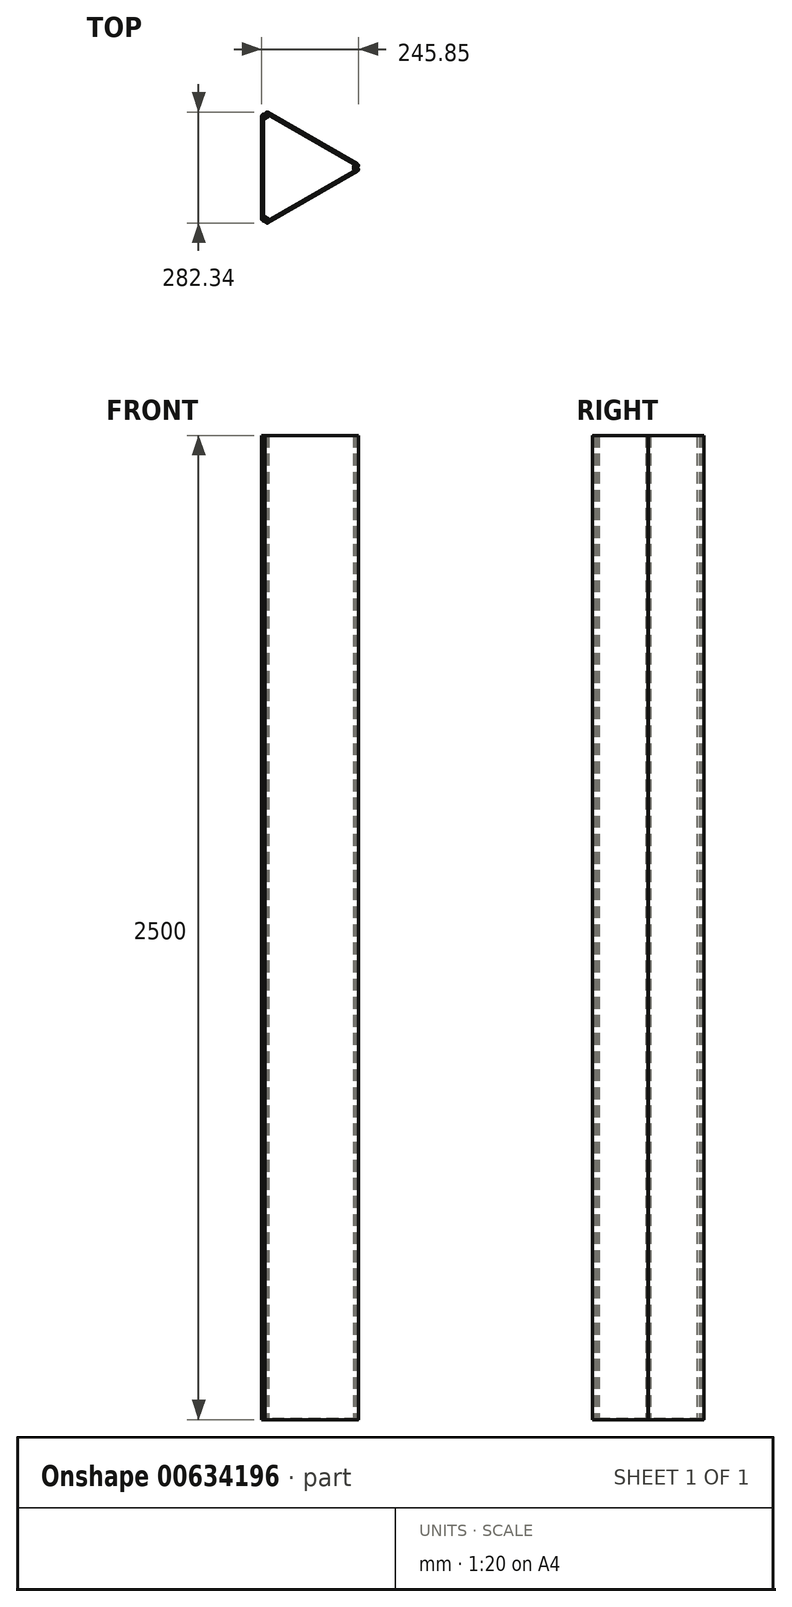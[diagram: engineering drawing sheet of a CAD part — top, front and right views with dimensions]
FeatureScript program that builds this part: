
annotation { "Feature Type Name" : "Feature", "Feature Type Description" : "" }
export const myFeature = defineFeature(function(context is Context, id is Id, definition is map)
    precondition{}
    {
        {
            var Q0;
            Q0=qCreatedBy(makeId("Top.planeOp"),FACE);
            var sketch = newSketch(context, id + "F0", { "sketchPlane" : qUnion([Q0])});
            skLineSegment(sketch, "E0", {"start": v(16.45, 140.5) * mm, "end": v(243.35, 9.5) * mm});
            skLineSegment(sketch, "E1", {"start": v(243.35, -9.5) * mm, "end": v(16.45, -140.5) * mm});
            skPoint(sketch, "E2.visualSharp", {"position": v(0, 150) * mm});
            skArc(sketch, "E2.filletArc", {"start": v(16.45, 140.5) * mm, "mid": v(10.42, 139.7) * mm, "end": v(9.62, 133.67) * mm});
            skLineSegment(sketch, "E3", {"start": v(0, -131) * mm, "end": v(0, 131) * mm});
            skArc(sketch, "E4.filletArc", {"start": v(9.33, 133.5) * mm, "mid": v(3.7, 135.83) * mm, "end": v(0, 131) * mm});
            skPoint(sketch, "E5.visualSharp", {"position": v(259.8, 0) * mm});
            skArc(sketch, "E5.filletArc", {"start": v(240.85, 0.17) * mm, "mid": v(245.68, 3.88) * mm, "end": v(243.35, 9.5) * mm});
            skPoint(sketch, "E6.visualSharp", {"position": v(0, -150) * mm});
            skArc(sketch, "E6.filletArc", {"start": v(0, -131) * mm, "mid": v(3.7, -135.83) * mm, "end": v(9.33, -133.5) * mm});
            skArc(sketch, "E7.filletArc", {"start": v(9.62, -133.67) * mm, "mid": v(10.42, -139.7) * mm, "end": v(16.45, -140.5) * mm});
            skArc(sketch, "E8.filletArc", {"start": v(243.35, -9.5) * mm, "mid": v(245.68, -3.88) * mm, "end": v(240.85, -0.17) * mm});
            skLineSegment(sketch, "E9", {"start": v(240.85, -0.17) * mm, "end": v(238.35, -0.17) * mm});
            skLineSegment(sketch, "E10", {"start": v(238.35, -0.17) * mm, "end": v(238.35, 0.17) * mm});
            skLineSegment(sketch, "E11", {"start": v(238.35, 0.17) * mm, "end": v(240.85, 0.17) * mm});
            skLineSegment(sketch, "E12", {"start": v(240.85, 5.17) * mm, "end": v(240.85, -5.17) * mm, "construction": true});
            skLineSegment(sketch, "E13", {"start": v(13.95, -136.17) * mm, "end": v(5, -131) * mm, "construction": true});
            skLineSegment(sketch, "E14", {"start": v(9.62, -133.67) * mm, "end": v(10.87, -131.5) * mm});
            skLineSegment(sketch, "E15", {"start": v(9.33, -133.5) * mm, "end": v(10.58, -131.33) * mm});
            skLineSegment(sketch, "E16", {"start": v(10.58, -131.33) * mm, "end": v(10.87, -131.5) * mm});
            skLineSegment(sketch, "E17", {"start": v(13.95, 136.17) * mm, "end": v(5, 131) * mm, "construction": true});
            skLineSegment(sketch, "E18", {"start": v(9.62, 133.67) * mm, "end": v(10.87, 131.5) * mm});
            skLineSegment(sketch, "E19", {"start": v(9.33, 133.5) * mm, "end": v(10.58, 131.33) * mm});
            skLineSegment(sketch, "E20", {"start": v(10.58, 131.33) * mm, "end": v(10.87, 131.5) * mm});
            skSolve(sketch);
        }
        {
            var Q0;
            Q0 = qSketchRegion(id + "F0", true);
            extrude(context, id + "F1", {"entities" : qUnion([Q0]), "depth" : 2500 * mm, "offsetDistance" : 25 * mm});
        }
        {
            var Q0;
            Q0=makeQuery(id+"F1.opExtrude","CAP_FACE",FACE,{"disambiguationData":[OSD([sQuery(id+"F0.wireOp",EDGE,"E0"),sQuery(id+"F0.wireOp",EDGE,"E1"),sQuery(id+"F0.wireOp",EDGE,"E2.filletArc"),sQuery(id+"F0.wireOp",EDGE,"E3"),sQuery(id+"F0.wireOp",EDGE,"E4.filletArc"),sQuery(id+"F0.wireOp",EDGE,"E5.filletArc"),sQuery(id+"F0.wireOp",EDGE,"E6.filletArc"),sQuery(id+"F0.wireOp",EDGE,"E7.filletArc"),sQuery(id+"F0.wireOp",EDGE,"E8.filletArc")])],"isStart":false});
            var Q1;
            Q1=makeQuery(id+"F1.opExtrude","CAP_FACE",FACE,{"disambiguationData":[OSD([sQuery(id+"F0.wireOp",EDGE,"E0"),sQuery(id+"F0.wireOp",EDGE,"E1"),sQuery(id+"F0.wireOp",EDGE,"E2.filletArc"),sQuery(id+"F0.wireOp",EDGE,"E3"),sQuery(id+"F0.wireOp",EDGE,"E4.filletArc"),sQuery(id+"F0.wireOp",EDGE,"E5.filletArc"),sQuery(id+"F0.wireOp",EDGE,"E6.filletArc"),sQuery(id+"F0.wireOp",EDGE,"E7.filletArc"),sQuery(id+"F0.wireOp",EDGE,"E8.filletArc")])],"isStart":true});
            var Q2;
            Q2=makeQuery(id+"F1.opExtrude","SWEPT_BODY",BODY,{"disambiguationData":[OSD([sQuery(id+"F0.wireOp",EDGE,"E0"),sQuery(id+"F0.wireOp",EDGE,"E1"),sQuery(id+"F0.wireOp",EDGE,"E2.filletArc"),sQuery(id+"F0.wireOp",EDGE,"E3"),sQuery(id+"F0.wireOp",EDGE,"E4.filletArc"),sQuery(id+"F0.wireOp",EDGE,"E5.filletArc"),sQuery(id+"F0.wireOp",EDGE,"E6.filletArc"),sQuery(id+"F0.wireOp",EDGE,"E7.filletArc"),sQuery(id+"F0.wireOp",EDGE,"E8.filletArc")])]});
            shell(context, id + "F2", {"entities" : qUnion([Q0, Q1]), "parts" : qUnion([Q2]), "thickness" : 5 * mm});
        }
        {
            var Q0;
            Q0=makeQuery(id+"F1.opExtrude","CAP_FACE",FACE,{"disambiguationData":[OSD([sQuery(id+"F0.wireOp",EDGE,"E0"),sQuery(id+"F0.wireOp",EDGE,"E1"),sQuery(id+"F0.wireOp",EDGE,"E2.filletArc"),sQuery(id+"F0.wireOp",EDGE,"E3"),sQuery(id+"F0.wireOp",EDGE,"E4.filletArc"),sQuery(id+"F0.wireOp",EDGE,"E5.filletArc"),sQuery(id+"F0.wireOp",EDGE,"E6.filletArc"),sQuery(id+"F0.wireOp",EDGE,"E7.filletArc"),sQuery(id+"F0.wireOp",EDGE,"E8.filletArc"),sQuery(id+"F0.wireOp",EDGE,"E9"),sQuery(id+"F0.wireOp",EDGE,"E10"),sQuery(id+"F0.wireOp",EDGE,"E11"),sQuery(id+"F0.wireOp",EDGE,"E14"),sQuery(id+"F0.wireOp",EDGE,"E15"),sQuery(id+"F0.wireOp",EDGE,"E16"),sQuery(id+"F0.wireOp",EDGE,"E18"),sQuery(id+"F0.wireOp",EDGE,"E19"),sQuery(id+"F0.wireOp",EDGE,"E20")])],"isStart":true});
            var sketch = newSketch(context, id + "F3", { "sketchPlane" : qUnion([Q0])});
            skLineSegment(sketch, "E21.0", {"start": v(5, 131) * mm, "end": v(5, -131) * mm});
            skLineSegment(sketch, "E21.1", {"start": v(5, -131) * mm, "end": v(8.75, -124.5) * mm});
            skLineSegment(sketch, "E21.2", {"start": v(8.75, -124.5) * mm, "end": v(17.7, -129.67) * mm});
            skLineSegment(sketch, "E21.3", {"start": v(13.95, -136.17) * mm, "end": v(17.7, -129.67) * mm});
            skLineSegment(sketch, "E21.4", {"start": v(13.95, -136.17) * mm, "end": v(240.85, -5.17) * mm});
            skLineSegment(sketch, "E21.5", {"start": v(233.35, -5.17) * mm, "end": v(240.85, -5.17) * mm});
            skLineSegment(sketch, "E21.6", {"start": v(233.35, 5.17) * mm, "end": v(233.35, -5.17) * mm});
            skLineSegment(sketch, "E21.7", {"start": v(240.85, 5.17) * mm, "end": v(233.35, 5.17) * mm});
            skLineSegment(sketch, "E21.8", {"start": v(240.85, 5.17) * mm, "end": v(13.95, 136.17) * mm});
            skLineSegment(sketch, "E21.9", {"start": v(5, 131) * mm, "end": v(8.75, 124.5) * mm});
            skLineSegment(sketch, "E21.10", {"start": v(8.75, 124.5) * mm, "end": v(17.7, 129.67) * mm});
            skLineSegment(sketch, "E21.11", {"start": v(13.95, 136.17) * mm, "end": v(17.7, 129.67) * mm});
            skPoint(sketch, "E21.12", {"position": v(6.87, -127.75) * mm});
            skPoint(sketch, "E21.13", {"position": v(15.83, -132.92) * mm});
            skSolve(sketch);
        }
        {
            var Q0;
            Q0 = qSketchRegion(id + "F3", true);
            extrude(context, id + "F4", {"entities" : qUnion([Q0]), "operationType" : NewBodyOperationType.ADD, "oppositeDirection" : true, "depth" : 2 * mm, "offsetDistance" : 25 * mm});
        }
    });
